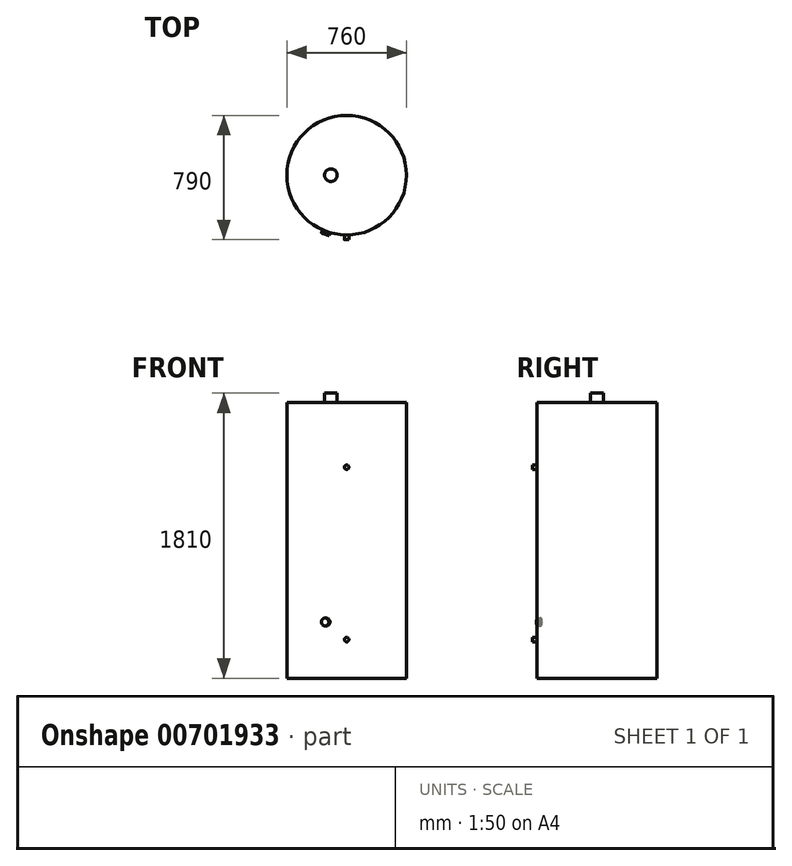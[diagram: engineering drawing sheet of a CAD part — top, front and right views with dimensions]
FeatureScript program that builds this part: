
annotation { "Feature Type Name" : "Feature", "Feature Type Description" : "" }
export const myFeature = defineFeature(function(context is Context, id is Id, definition is map)
    precondition{}
    {
        {
            var Q0;
            Q0=qCreatedBy(makeId("Top.planeOp"),FACE);
            var sketch = newSketch(context, id + "F0", { "sketchPlane" : qUnion([Q0])});
            skCircle(sketch, "E0", {"center": v(0, 0) * mm, "radius": 380 * mm});
            skSolve(sketch);
        }
        {
            var Q0;
            Q0=makeQuery(id+"F0.imprint","IMPRINT",FACE,{"disambiguationData":[TD([[makeQuery(id+"F0.imprint","IMPRINT",EDGE,{"derivedFrom":sQuery(id+"F0.wireOp",EDGE,"E0")}),1.0]])]});
            extrude(context, id + "F1", {"entities" : qUnion([Q0]), "depth" : 1750 * mm, "offsetDistance" : 25 * mm});
        }
        {
            var Q0;
            Q0=qCreatedBy(makeId("Front.planeOp"),FACE);
            var sketch = newSketch(context, id + "F2", { "sketchPlane" : qUnion([Q0])});
            skCircle(sketch, "E1", {"center": v(0, 245) * mm, "radius": 14 * mm});
            skCircle(sketch, "E2", {"center": v(0, 1340) * mm, "radius": 14 * mm});
            skSolve(sketch);
        }
        {
            var Q0;
            Q0 = qSketchRegion(id + "F2", true);
            extrude(context, id + "F3", {"entities" : qUnion([Q0]), "operationType" : NewBodyOperationType.ADD, "depth" : 410 * mm, "offsetDistance" : 25 * mm});
        }
        {
            var Q0;
            Q0=makeQuery(id+"F1.opExtrude","CAP_FACE",FACE,{"disambiguationData":[OSD([sQuery(id+"F0.wireOp",EDGE,"E0")])],"isStart":false});
            var sketch = newSketch(context, id + "F4", { "sketchPlane" : qUnion([Q0])});
            skCircle(sketch, "E3", {"center": v(-100, 0) * mm, "radius": 40 * mm});
            skSolve(sketch);
        }
        {
            var Q0;
            Q0=makeQuery(id+"F4.imprint","IMPRINT",FACE,{"disambiguationData":[TD([[makeQuery(id+"F4.imprint","IMPRINT",EDGE,{"derivedFrom":sQuery(id+"F4.wireOp",EDGE,"E3")}),1.0]])]});
            extrude(context, id + "F5", {"entities" : qUnion([Q0]), "operationType" : NewBodyOperationType.ADD, "depth" : 60 * mm, "offsetDistance" : 25 * mm});
        }
        {
            var Q0;
            Q0=qCreatedBy(makeId("Front.planeOp"),FACE);
            var sketch = newSketch(context, id + "F6", { "sketchPlane" : qUnion([Q0])});
            skLineSegment(sketch, "E4", {"start": v(0, 0) * mm, "end": v(0, 2496.38) * mm});
            skSolve(sketch);
        }
        {
            var Q0;
            Q0=qCreatedBy(makeId("Front.planeOp"),FACE);
            var Q1;
            Q1=sQuery(id+"F6.wireOp",EDGE,"E4");
            cPlane(context, id + "F7", {"entities" : qUnion([Q0, Q1]), "cplaneType" : CPlaneType.LINE_ANGLE, "offset" : 25 * mm, "angle" : 20 * degree, "oppositeDirection" : true, "width" : 150 * mm, "height" : 150 * mm});
        }
        {
            var Q0;
            Q0=qCreatedBy(id+"F7.planeOp",FACE);
            var sketch = newSketch(context, id + "F8", { "sketchPlane" : qUnion([Q0])});
            skCircle(sketch, "E5", {"center": v(0, 357) * mm, "radius": 25 * mm});
            skSolve(sketch);
        }
        {
            var Q0;
            Q0 = qSketchRegion(id + "F8", true);
            extrude(context, id + "F9", {"entities" : qUnion([Q0]), "operationType" : NewBodyOperationType.ADD, "oppositeDirection" : true, "depth" : 400 * mm, "offsetDistance" : 25 * mm});
        }
    });
